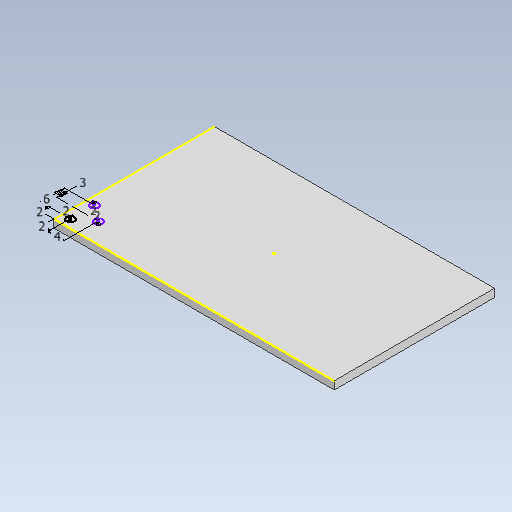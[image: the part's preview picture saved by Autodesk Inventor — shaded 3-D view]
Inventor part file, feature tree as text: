
AUTODESK INVENTOR PART (.ipt)
format: ipt  version: 2020 (Build 240168000, 168)  size: 104,448 bytes
history: native  units: mm
features: sketch x2, extrude x1
ambient origin geometry x8: Origin, YZ Plane, XZ Plane, XY Plane, X Axis, Y Axis, Z Axis, Center Point
bodies: Solid1 (feature_tree)
feature tree (3):
  extrude  "Extrusion1"  Depth=40.0mm
  sketch  "Sketch2"  dims[d2=2.0mm d3=0.0mm d4=2.0mm d5=2.0mm d6=2.0mm d7=2.0mm d8=6.0mm d9=2.0mm d11=4.0mm d12=3.0mm]
  sketch  "Sketch1"  dims[d0=70.0mm d1=40.0mm]
